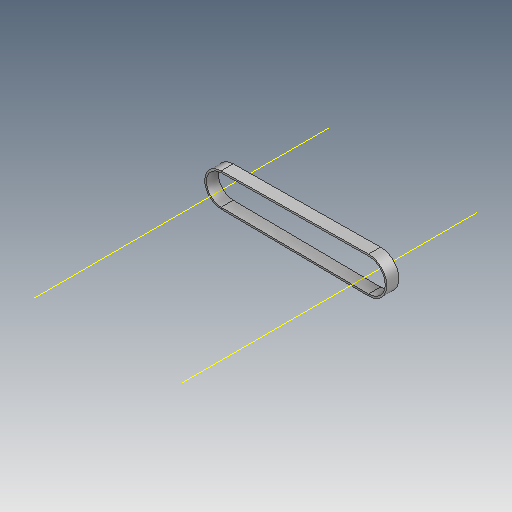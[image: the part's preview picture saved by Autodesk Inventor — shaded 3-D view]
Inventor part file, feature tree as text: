
AUTODESK INVENTOR PART (.ipt)
format: ipt  version: 2020.3 (Build 243373010, 373A)  size: 106,496 bytes
history: native  units: mm (DEFAULTED — no unit token found)
features: other x4, plane x2, sketch x1, sweep x1
ambient origin geometry x8: Origin, YZ Plane, XZ Plane, XY Plane, X Axis, Y Axis, Z Axis, Center Point
bodies: Solid1 (feature_tree)
feature tree (8):
  sketch  "Sketch Path"  dims[d0=12.0mm d2=0.0mm d4=0.381mm d5=1.27mm d6=0.0mm d7=0.0mm d8=0.0mm d9=0.0mm d10=0.0mm d11=0.0mm]
  other  "Cross Section Plane"
  other  "Work Axis1"
  other  "Work Axis2"
  plane  "Work Plane2"
  plane  "Work Plane3"
  sweep  "Belt"
  other  "Cross Section"
